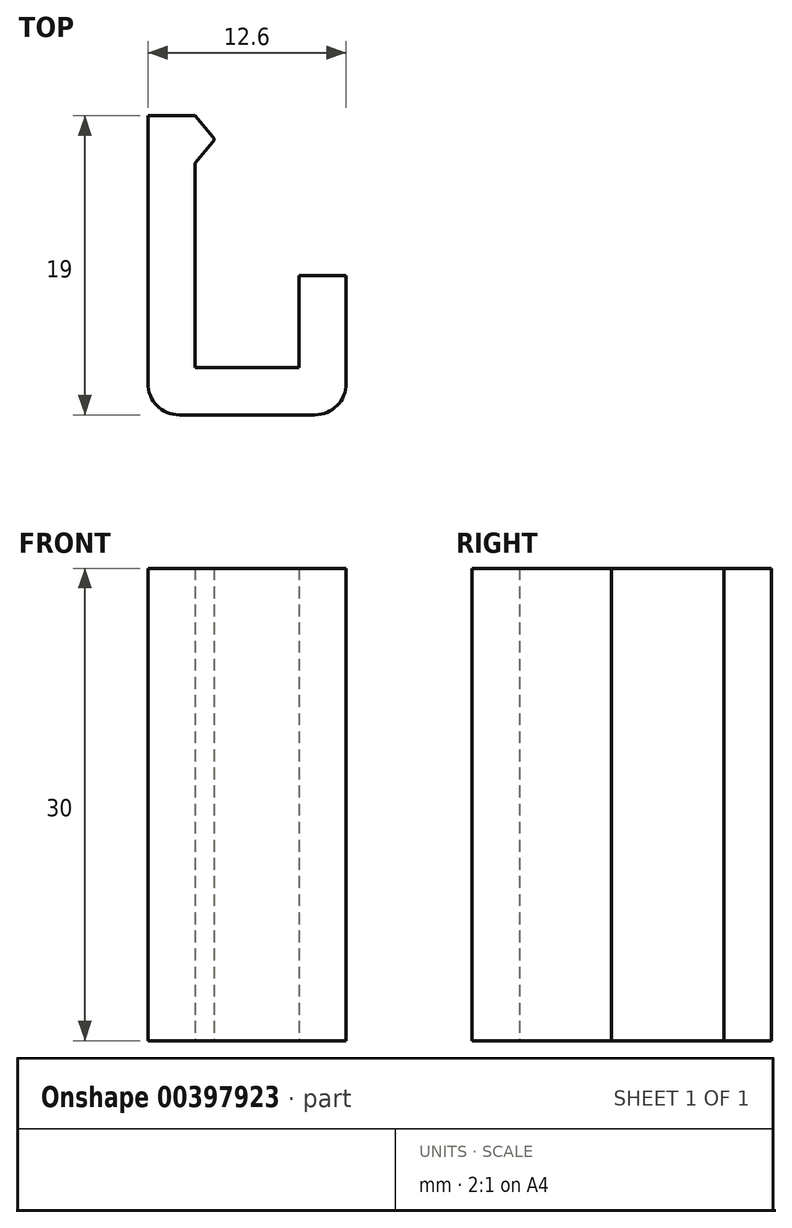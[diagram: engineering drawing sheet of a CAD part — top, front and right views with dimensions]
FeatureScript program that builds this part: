
annotation { "Feature Type Name" : "Feature", "Feature Type Description" : "" }
export const myFeature = defineFeature(function(context is Context, id is Id, definition is map)
    precondition{}
    {
        {
            var Q0;
            Q0=qCreatedBy(makeId("Top.planeOp"),FACE);
            var sketch = newSketch(context, id + "F0", { "sketchPlane" : qUnion([Q0])});
            skLineSegment(sketch, "E0", {"start": v(-12.6, 19) * mm, "end": v(-12.6, 2) * mm});
            skLineSegment(sketch, "E1", {"start": v(-10.6, 0) * mm, "end": v(-2, 0) * mm});
            skLineSegment(sketch, "E2", {"start": v(0, 2) * mm, "end": v(0, 8.85) * mm});
            skLineSegment(sketch, "E3.0", {"start": v(-3, 3) * mm, "end": v(-3, 8.85) * mm});
            skLineSegment(sketch, "E3.1", {"start": v(-9.6, 3) * mm, "end": v(-3, 3) * mm});
            skLineSegment(sketch, "E3.2", {"start": v(-9.6, 16) * mm, "end": v(-9.6, 3) * mm});
            skLineSegment(sketch, "E4", {"start": v(-3, 8.85) * mm, "end": v(0, 8.85) * mm});
            skLineSegment(sketch, "E5", {"start": v(-9.6, 19) * mm, "end": v(-8.45, 17.63) * mm});
            skLineSegment(sketch, "E6", {"start": v(-8.45, 17.37) * mm, "end": v(-9.6, 16) * mm});
            skPoint(sketch, "E7.visualSharp", {"position": v(-8.34, 17.5) * mm});
            skArc(sketch, "E7.filletArc", {"start": v(-8.45, 17.37) * mm, "mid": v(-8.4, 17.5) * mm, "end": v(-8.45, 17.63) * mm});
            skLineSegment(sketch, "E8", {"start": v(-8.4, 29.06) * mm, "end": v(-8.4, 27.06) * mm, "construction": true});
            skLineSegment(sketch, "E9", {"start": v(-12.6, 19) * mm, "end": v(-9.6, 19) * mm});
            skPoint(sketch, "E10.visualSharp", {"position": v(-12.6, 0) * mm});
            skArc(sketch, "E10.filletArc", {"start": v(-12.6, 2) * mm, "mid": v(-12.01, 0.59) * mm, "end": v(-10.6, 0) * mm});
            skPoint(sketch, "E11.visualSharp", {"position": v(0, 0) * mm});
            skArc(sketch, "E11.filletArc", {"start": v(-2, 0) * mm, "mid": v(-0.59, 0.59) * mm, "end": v(0, 2) * mm});
            skSolve(sketch);
        }
        {
            var Q0;
            Q0=qSketchRegion(id+"F0",true);
            extrude(context, id + "F1", {"entities" : qUnion([Q0]), "depth" : 30 * mm});
        }
    });
